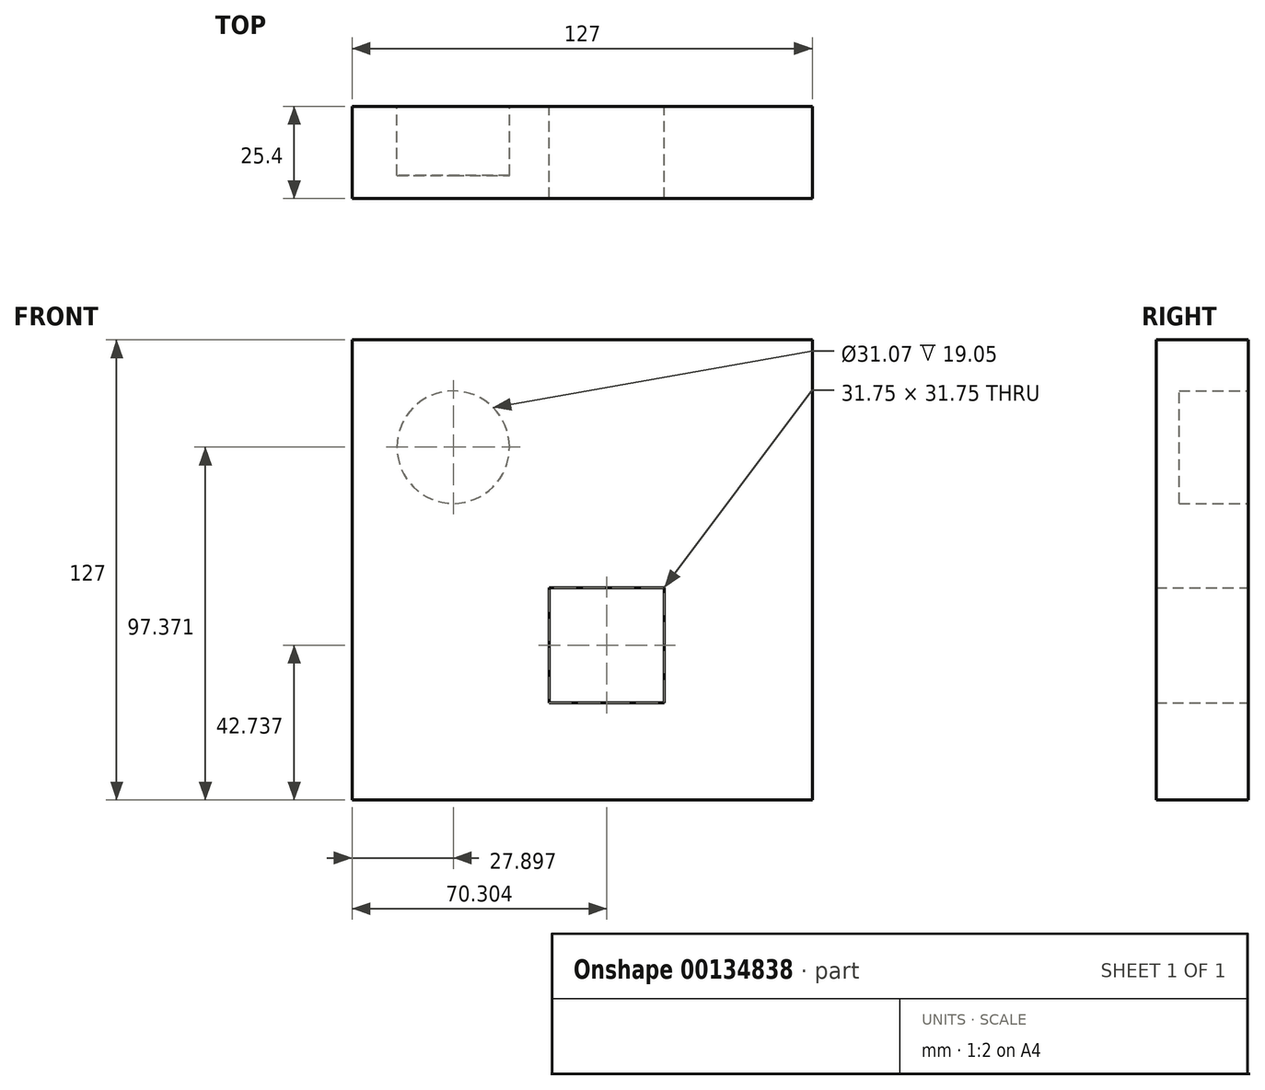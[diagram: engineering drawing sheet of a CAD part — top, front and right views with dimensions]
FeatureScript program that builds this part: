
annotation { "Feature Type Name" : "Feature", "Feature Type Description" : "" }
export const myFeature = defineFeature(function(context is Context, id is Id, definition is map)
    precondition{}
    {
        {
            var Q0;
            Q0=qCreatedBy(makeId("Front.planeOp"),FACE);
            var sketch = newSketch(context, id + "F0", { "sketchPlane" : qUnion([Q0])});
            skLineSegment(sketch, "E0.bottom", {"start": v(63.5, -63.5) * mm, "end": v(-63.5, -63.5) * mm});
            skLineSegment(sketch, "E0.top", {"start": v(63.5, 63.5) * mm, "end": v(-63.5, 63.5) * mm});
            skLineSegment(sketch, "E0.left", {"start": v(63.5, -63.5) * mm, "end": v(63.5, 63.5) * mm});
            skLineSegment(sketch, "E0.right", {"start": v(-63.5, -63.5) * mm, "end": v(-63.5, 63.5) * mm});
            skPoint(sketch, "E0.middle", {"position": v(0, 0) * mm});
            skCircle(sketch, "E1", {"center": v(-35.6, 33.87) * mm, "radius": 15.53 * mm});
            skLineSegment(sketch, "E2.bottom", {"start": v(22.68, -36.64) * mm, "end": v(-9.07, -36.64) * mm});
            skLineSegment(sketch, "E2.top", {"start": v(22.68, -4.89) * mm, "end": v(-9.07, -4.89) * mm});
            skLineSegment(sketch, "E2.left", {"start": v(22.68, -36.64) * mm, "end": v(22.68, -4.89) * mm});
            skLineSegment(sketch, "E2.right", {"start": v(-9.07, -36.64) * mm, "end": v(-9.07, -4.89) * mm});
            skPoint(sketch, "E2.middle", {"position": v(6.8, -20.76) * mm});
            skSolve(sketch);
        }
        {
            var Q0;
            Q0 = qSketchRegion(id + "F0", true);
            extrude(context, id + "F1", {"entities" : qUnion([Q0]), "depth" : 25.4 * mm});
        }
        {
            var Q0;
            Q0=makeQuery(id+"F1.opExtrude","CAP_FACE",FACE,{"disambiguationData":[OSD([sQuery(id+"F0.wireOp",EDGE,"E0.bottom"),sQuery(id+"F0.wireOp",EDGE,"E0.top"),sQuery(id+"F0.wireOp",EDGE,"E0.left"),sQuery(id+"F0.wireOp",EDGE,"E0.right"),sQuery(id+"F0.wireOp",EDGE,"E1")])],"isStart":false});
            var sketch = newSketch(context, id + "F2", { "sketchPlane" : qUnion([Q0])});
            skCircle(sketch, "E3", {"center": v(-35.6, 33.87) * mm, "radius": 23.88 * mm});
            skSolve(sketch);
        }
        {
            var Q0;
            Q0 = qSketchRegion(id + "F2", true);
            extrude(context, id + "F3", {"entities" : qUnion([Q0]), "operationType" : NewBodyOperationType.REMOVE, "oppositeDirection" : true, "depth" : 6.35 * mm});
        }
        {
            var Q0;
            Q0 = qSketchRegion(id + "F0", true);
            extrude(context, id + "F4", {"entities" : qUnion([Q0]), "operationType" : NewBodyOperationType.ADD, "depth" : 25.4 * mm});
        }
        {
            var Q0;
            {var subQ0=sQuery(id+"F0.wireOp",EDGE,"E2.right");var subQ1=sQuery(id+"F0.wireOp",EDGE,"E2.left");var subQ2=sQuery(id+"F0.wireOp",EDGE,"E2.top");var subQ3=sQuery(id+"F0.wireOp",EDGE,"E2.bottom");var subQ4=sQuery(id+"F0.wireOp",EDGE,"E1");var subQ5=sQuery(id+"F0.wireOp",EDGE,"E0.right");var subQ6=sQuery(id+"F0.wireOp",EDGE,"E0.left");var subQ7=sQuery(id+"F0.wireOp",EDGE,"E0.top");var subQ8=sQuery(id+"F0.wireOp",EDGE,"E0.bottom");Q0=makeQuery(id+"F4.boolean.opBoolean","MERGE",FACE,{"derivedFrom":[makeQuery(id+"F1.opExtrude","CAP_FACE",FACE,{"disambiguationData":[OSD([subQ8,subQ7,subQ6,subQ5,subQ4,subQ3,subQ2,subQ1,subQ0])],"isStart":false}),makeQuery(id+"F4.opExtrude","CAP_FACE",FACE,{"disambiguationData":[OSD([subQ8,subQ7,subQ6,subQ5,subQ4,subQ3,subQ2,subQ1,subQ0])],"isStart":false})]});}
            var sketch = newSketch(context, id + "F5", { "sketchPlane" : qUnion([Q0])});
            skLineSegment(sketch, "E4.bottom", {"start": v(41.73, -39.81) * mm, "end": v(3.63, -39.81) * mm});
            skLineSegment(sketch, "E4.top", {"start": v(41.73, -1.71) * mm, "end": v(3.63, -1.71) * mm});
            skLineSegment(sketch, "E4.left", {"start": v(41.73, -39.81) * mm, "end": v(41.73, -1.71) * mm});
            skLineSegment(sketch, "E4.right", {"start": v(3.63, -39.81) * mm, "end": v(3.63, -1.71) * mm});
            skPoint(sketch, "E4.middle", {"position": v(22.68, -20.76) * mm});
            skSolve(sketch);
        }
        {
            var Q0;
            {var subQ5=sQuery(id+"F5.wireOp",EDGE,"E4.bottom");Q0=makeQuery(id+"F5.imprint","IMPRINT",FACE,{"disambiguationData":[TD([[makeQuery(id+"F5.imprint","IMPRINT",EDGE,{"derivedFrom":subQ5}),1.0]])]});}
            var sketch = newSketch(context, id + "F6", { "sketchPlane" : qUnion([Q0])});
            skCircle(sketch, "E5", {"center": v(-35.6, 33.87) * mm, "radius": 25.36 * mm});
            skSolve(sketch);
        }
        {
            var Q0;
            Q0 = qSketchRegion(id + "F6", true);
            extrude(context, id + "F7", {"entities" : qUnion([Q0]), "operationType" : NewBodyOperationType.ADD, "oppositeDirection" : true, "depth" : 6.35 * mm});
        }
    });
